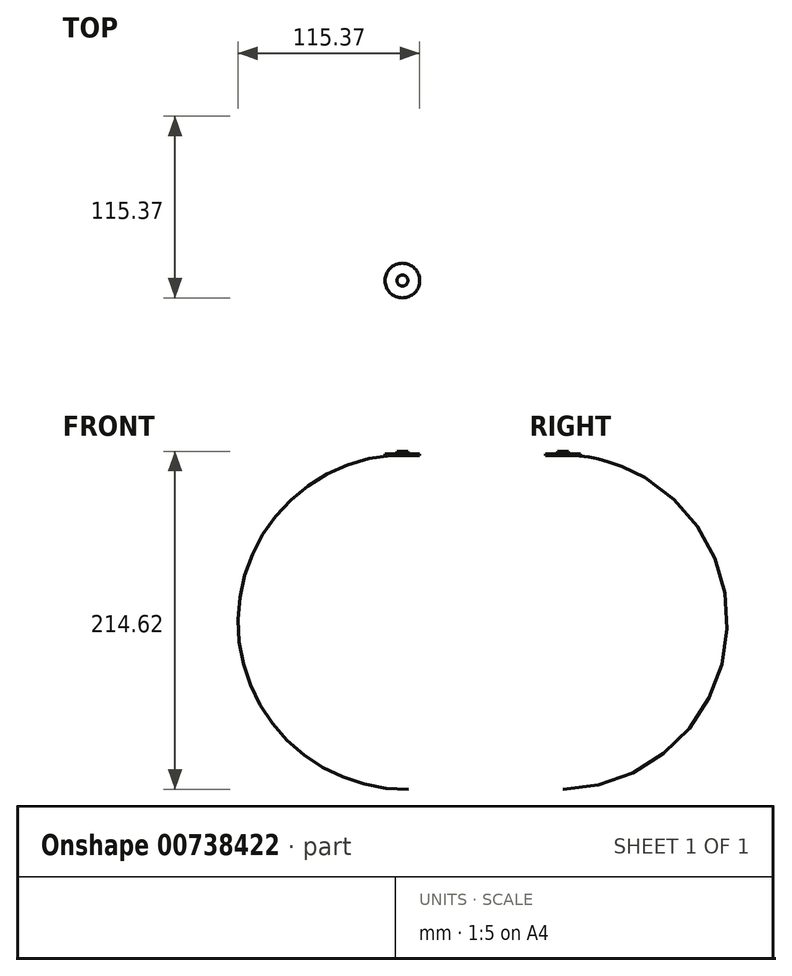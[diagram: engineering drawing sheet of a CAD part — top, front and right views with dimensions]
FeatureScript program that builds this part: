
annotation { "Feature Type Name" : "Feature", "Feature Type Description" : "" }
export const myFeature = defineFeature(function(context is Context, id is Id, definition is map)
    precondition{}
    {
        {
            var Q0;
            Q0=qCreatedBy(makeId("Right.planeOp"),FACE);
            var sketch = newSketch(context, id + "F0", { "sketchPlane" : qUnion([Q0])});
            skLineSegment(sketch, "E0", {"start": v(0, 2.5) * mm, "end": v(3.5, 2.5) * mm});
            skLineSegment(sketch, "E1", {"start": v(3.5, 2.5) * mm, "end": v(3.5, 0.75) * mm});
            skLineSegment(sketch, "E2", {"start": v(11, 0) * mm, "end": v(11, 0.75) * mm});
            skLineSegment(sketch, "E3", {"start": v(11, 0.75) * mm, "end": v(3.5, 0.75) * mm});
            skArc(sketch, "E4", {"start": v(11, 0) * mm, "mid": v(5.5, 0.33) * mm, "end": v(0, 0.38) * mm});
            skLineSegment(sketch, "E5", {"start": v(0, 2.5) * mm, "end": v(0, 0.38) * mm});
            skSolve(sketch);
        }
        {
            var Q0;
            Q0 = qSketchRegion(id + "F0", true);
            var Q1;
            Q1=sQuery(id+"F0.wireOp",EDGE,"E5");
            revolve(context, id + "F1", {"surfaceOperationType" : NewSurfaceOperationType.NEW, "entities" : qUnion([Q0]), "axis" : qUnion([Q1]), "revolveType" : RevolveType.FULL});
        }
    });
